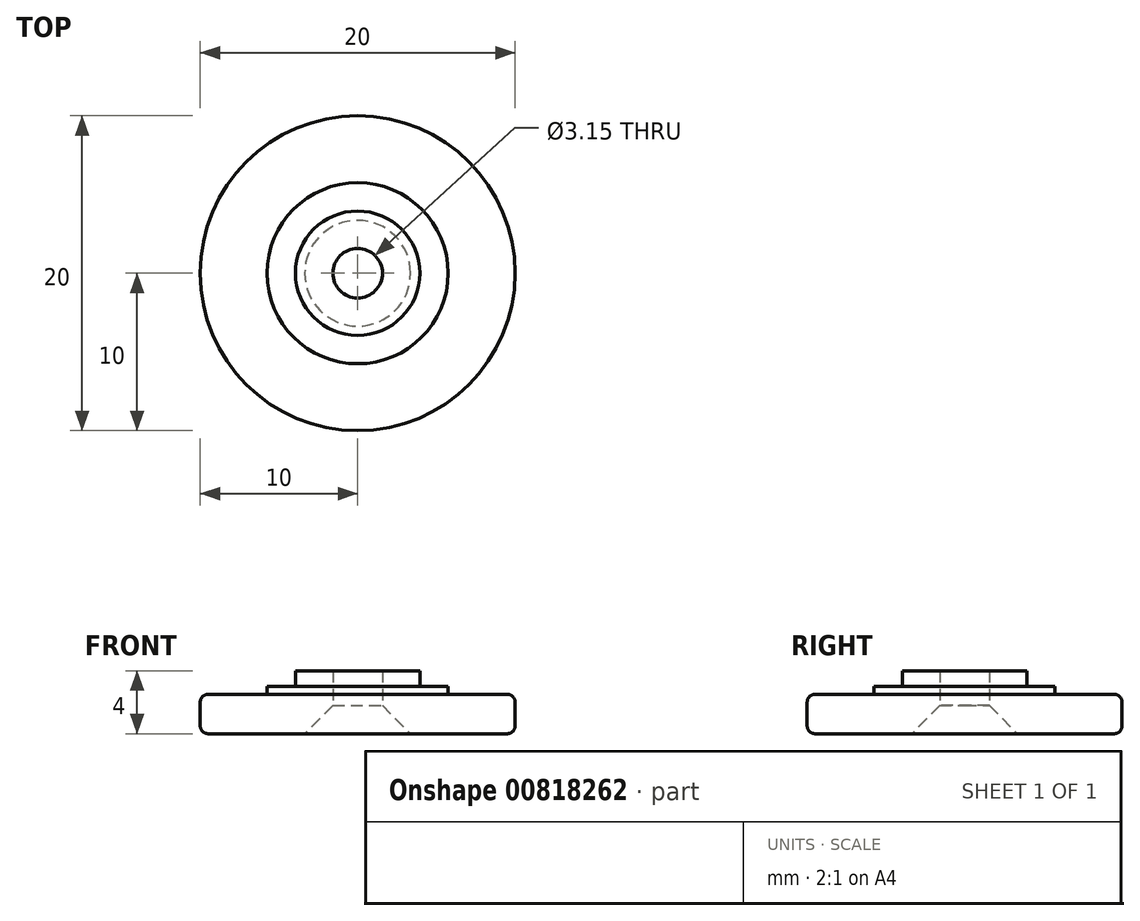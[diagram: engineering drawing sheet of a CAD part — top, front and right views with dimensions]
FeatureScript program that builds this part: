
annotation { "Feature Type Name" : "Feature", "Feature Type Description" : "" }
export const myFeature = defineFeature(function(context is Context, id is Id, definition is map)
    precondition{}
    {
        {
            var Q0;
            Q0=qCreatedBy(makeId("Top.planeOp"),FACE);
            var sketch = newSketch(context, id + "F0", { "sketchPlane" : qUnion([Q0])});
            skCircle(sketch, "E0", {"center": v(0, 0) * mm, "radius": 10 * mm});
            skSolve(sketch);
        }
        {
            var Q0;
            Q0=makeQuery(id+"F0.imprint","IMPRINT",FACE,{"disambiguationData":[TD([[makeQuery(id+"F0.imprint","IMPRINT",EDGE,{"derivedFrom":sQuery(id+"F0.wireOp",EDGE,"E0")}),1.0]])]});
            extrude(context, id + "F1", {"entities" : qUnion([Q0]), "depth" : 2.5 * mm, "offsetDistance" : 25 * mm});
        }
        {
            var Q0;
            Q0=makeQuery(id+"F1.opExtrude","CAP_FACE",FACE,{"disambiguationData":[OSD([sQuery(id+"F0.wireOp",EDGE,"E0"),sQuery(id+"F0.wireOp",EDGE,"6NsyKhDP-W1GV-n0ri-Q7OR-qJNevtQDqUuP")])],"isStart":false});
            var sketch = newSketch(context, id + "F2", { "sketchPlane" : qUnion([Q0])});
            skCircle(sketch, "E1", {"center": v(0, 0) * mm, "radius": 5.75 * mm});
            skCircle(sketch, "E2", {"center": v(0, 0) * mm, "radius": 3.95 * mm});
            skSolve(sketch);
        }
        {
            var Q0;
            Q0=makeQuery(id+"F2.imprint","IMPRINT",FACE,{"disambiguationData":[TD([[makeQuery(id+"F2.imprint","IMPRINT",EDGE,{"derivedFrom":sQuery(id+"F2.wireOp",EDGE,"E2")}),1.0]])]});
            extrude(context, id + "F3", {"entities" : qUnion([Q0]), "operationType" : NewBodyOperationType.ADD, "depth" : 1.5 * mm, "offsetDistance" : 25 * mm});
        }
        {
            var Q0;
            Q0=qSketchRegion(id+"F2",true);
            extrude(context, id + "F4", {"entities" : qUnion([Q0]), "operationType" : NewBodyOperationType.ADD, "depth" : 0.5 * mm, "offsetDistance" : 25 * mm});
        }
        {
            var Q0;
            Q0=makeQuery(id+"F1.opExtrude","CAP_EDGE",EDGE,{"disambiguationData":[OSD([sQuery(id+"F0.wireOp",EDGE,"E0")])],"isStart":true});
            var Q1;
            Q1=makeQuery(id+"F1.opExtrude","CAP_EDGE",EDGE,{"disambiguationData":[OSD([sQuery(id+"F0.wireOp",EDGE,"E0")])],"isStart":false});
            fillet(context, id + "F5", {"entities" : qUnion([Q0, Q1]), "radius" : 0.5 * mm, "tangentPropagation" : true, "allowEdgeOverflow" : false});
        }
        {
            var Q0;
            Q0=sQuery(id+"F0.wireOp",VERTEX,"E0.center");
            var Q1;
            Q1=makeQuery(id+"F1.opExtrude","SWEPT_BODY",BODY,{"disambiguationData":[OSD([sQuery(id+"F0.wireOp",EDGE,"E0")])]});
            hole(context, id + "F6", {"style" : HoleStyle.C_SINK, "endStyle" : HoleEndStyle.THROUGH, "oppositeDirection" : true, "standardTappedOrClearance" : lookupTablePath({ "standard" : "ISO", "fit" : "Close", "size" : "M3", "type" : "Clearance" }), "standardBlindInLast" : lookupTablePath({ "fit" : "Close", "standard" : "ISO", "size" : "M3", "type" : "Clearance" }), "holeDiameter" : 3.15 * mm, "cSinkDiameter" : 6.72 * mm, "cSinkAngle" : 90 * degree, "majorDiameter" : 5 * mm, "isTappedThrough" : true, "tappedDepth" : 12 * mm, "tapClearance" : 3, "startFromSketch" : true, "locations" : qUnion([Q0]), "scope" : qUnion([Q1])});
        }
    });
